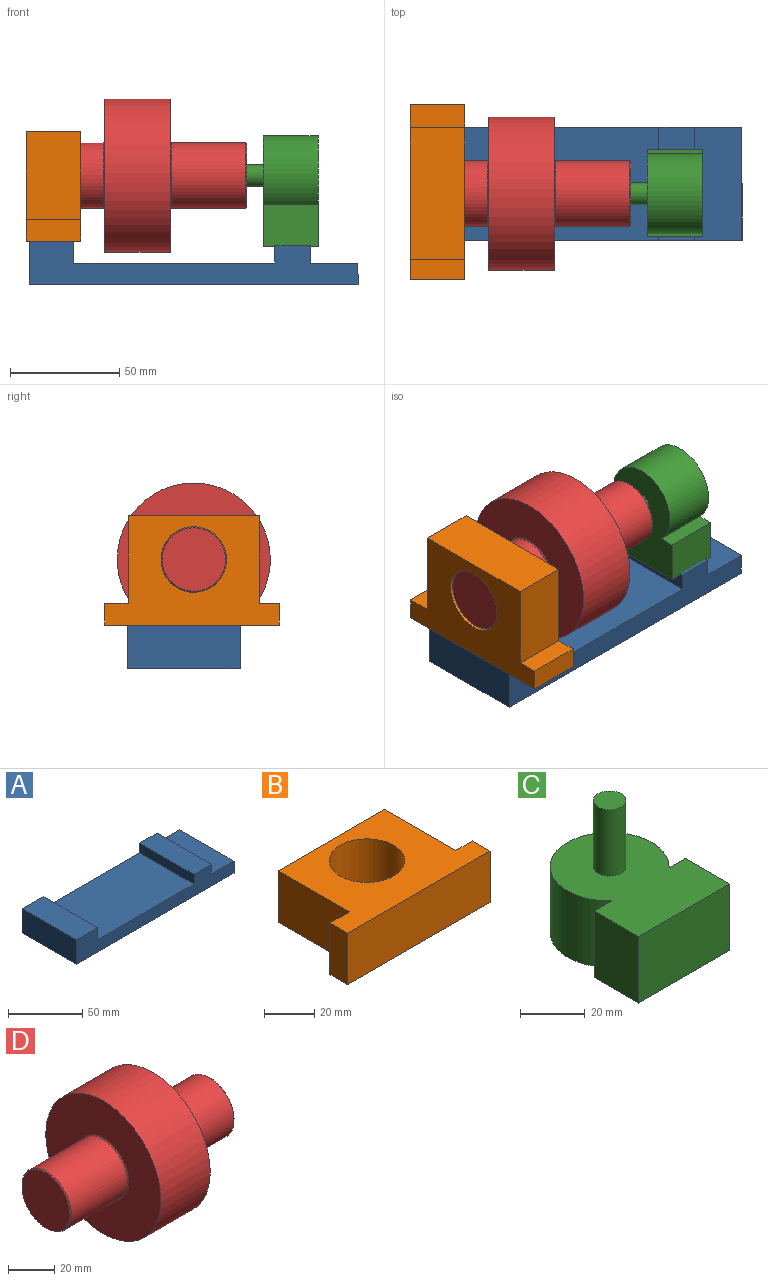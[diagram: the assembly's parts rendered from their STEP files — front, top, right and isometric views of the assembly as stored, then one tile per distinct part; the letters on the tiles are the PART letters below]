
ASSEMBLY  parts=4 mates=3
PART A: 12 faces, bbox 150.1x51.6x20 mm
  f0: plane 51.58x21.57mm, normal (0,0,1), area 1112.8mm2, adj f2,f3,f5,f10
  f1: plane 91.89x51.58mm, normal (0,0,1), area 4739.4mm2, adj f3,f5,f7,f9
  f2: plane 51.58x10mm, normal (1,0,0), area 515.8mm2, adj f0,f3,f5,f6
  f3: plane 150.07x20mm, normal (0,1,0), area 1833.9mm2, adj f0,f1,f2,f4,f6,f7,f8,f9
  f4: plane 51.58x20mm, normal (-1,0,0), area 1031.6mm2, adj f3,f5,f6,f8
  f5: plane 150.07x20mm, normal (0,-1,0), area 1833.9mm2, adj f0,f1,f2,f4,f6,f7,f8,f9
  f6: plane 150.07x51.58mm, normal (0,0,-1), area 7740.7mm2, adj f2,f3,f4,f5
  f7: plane 51.58x10mm, normal (1,0,0), area 515.8mm2, adj f1,f3,f5,f8
  f8: plane 51.58x20.17mm, normal (0,0,1), area 1040.1mm2, adj f3,f4,f5,f7
  f9: plane 51.58x8mm, normal (-1,0,0), area 412.6mm2, adj f1,f3,f5,f11
  f10: plane 51.58x8mm, normal (1,0,0), area 412.6mm2, adj f0,f3,f5,f11
  f11: plane 51.58x16.45mm, normal (0,0,1), area 848.3mm2, adj f3,f5,f9,f10
PART B: 11 faces, bbox 80x50x25 mm
  f0: plane 40x25mm, normal (-1,0,0), area 1000mm2, adj f1,f7,f9,f10
  f1: plane 25x10.8mm, normal (0,1,0), area 270.1mm2, adj f0,f2,f9,f10
  f2: plane 25x10mm, normal (-1,0,0), area 250mm2, adj f1,f3,f9,f10
  f3: plane 80x25mm, normal (0,-1,0), area 2000mm2, adj f2,f4,f9,f10
  f4: plane 25x10mm, normal (1,0,0), area 250mm2, adj f3,f5,f9,f10
  f5: plane 25x9.2mm, normal (0,1,0), area 229.9mm2, adj f4,f6,f9,f10
  f6: plane 40x25mm, normal (1,0,0), area 1000mm2, adj f5,f7,f9,f10
  f7: plane 60x25mm, normal (0,1,0), area 1500mm2, adj f0,f6,f9,f10
  f8: cylinder r=15mm len=30mm, axis (0,0,-1), area 2356.2mm2, adj f9,f10
  f9: plane 80x50mm, normal (0,0,1), area 2493.1mm2, adj f0,f1,f2,f3,f4,f5,f6,f7
  f10: plane 80x50mm, normal (0,0,-1), area 2493.1mm2, adj f0,f1,f2,f3,f4,f5,f6,f7
PART C: 10 faces, bbox 39.7x51x50 mm
  f0: plane 25x7.56mm, normal (0,1,0), area 189mm2, adj f1,f5,f6,f7
  f1: plane 25x19.32mm, normal (-1,0,0), area 482.9mm2, adj f0,f2,f6,f7
  f2: plane 39.69x25mm, normal (0,-1,0), area 992.3mm2, adj f1,f3,f6,f7
  f3: plane 25x19.32mm, normal (1,0,0), area 482.9mm2, adj f2,f4,f6,f7
  f4: plane 25x7.1mm, normal (0,1,0), area 177.5mm2, adj f3,f5,f6,f7
  f5: cylinder r=18.3mm len=36.6mm, axis (0,0,-1), area 2185mm2, adj f0,f4,f6,f7
  f6: plane 50.96x39.69mm, normal (0,0,1), area 1654.9mm2, adj f0,f1,f2,f3,f4,f5,f8
  f7: plane 50.96x39.69mm, normal (0,0,-1), area 1733.4mm2, adj f0,f1,f2,f3,f4,f5
  f8: cylinder r=5mm len=25mm, axis (0,0,-1), area 785.4mm2, adj f6,f9
  f9: plane 10x10mm, normal (0,0,1), area 78.5mm2, adj f8
PART D: 14 faces, bbox 100x70x70 mm
  f0: plane 29x29mm, normal (-1,0,0), area 660.5mm2, adj f10
  f1: plane 29x29mm, normal (1,0,0), area 565.5mm2, adj f9,f13
  f2: cylinder r=15mm len=34mm, axis (-1,0,0), area 3204.4mm2, adj f7,f9
  f3: plane 70x70mm, normal (1,0,0), area 3093.7mm2, adj f4,f7
  f4: cylinder r=35mm len=70mm, axis (-1,0,0), area 6597.3mm2, adj f3,f5
  f5: plane 70x70mm, normal (-1,0,0), area 3093.7mm2, adj f4,f8
  f6: cylinder r=15mm len=34mm, axis (-1,0,0), area 3204.4mm2, adj f8,f10
  f7: torus R=15.5mm, axis (1,0,0), area 74.9mm2, adj f2,f3
  f8: torus R=15.5mm, axis (-1,0,0), area 74.9mm2, adj f5,f6
  f9: cone r=15mm half-angle=45deg, axis (-1,0,0), area 65.5mm2, adj f1,f2
  f10: cone r=14.5mm half-angle=45deg, axis (1,0,0), area 65.5mm2, adj f0,f6
  f11: cylinder r=5mm len=29.5mm, axis (1,0,0), area 926.8mm2, adj f12,f13
  f12: plane 10x10mm, normal (1,0,0), area 78.5mm2, adj f11
  f13: cone r=5mm half-angle=45deg, axis (1,0,0), area 23.3mm2, adj f1,f11
PLACE A t=(47.23,10.87,-24.59)mm
PLACE B rot(axis=(0.58,-0.58,-0.58),120deg) t=(-4.55,-24.11,22.84)mm
PLACE C rot(axis=(0.58,-0.58,-0.58),120deg) t=(104.02,-27.9,54.62)mm
PLACE D rot(axis=(-1,0,0),180deg) t=(22.01,-5.68,25.41)mm
MATE cylindrical D.f2 <-> C.f5  axis (-1,0,0) through (53.93,6.26,25.41)mm
MATE planar A.f8 <-> B.f3  axis (0,0,1) through (-17.73,10.87,-4.59)mm
MATE cylindrical B.f8 <-> D.f2  axis (-1,0,0) through (-29.55,6.26,25.41)mm
